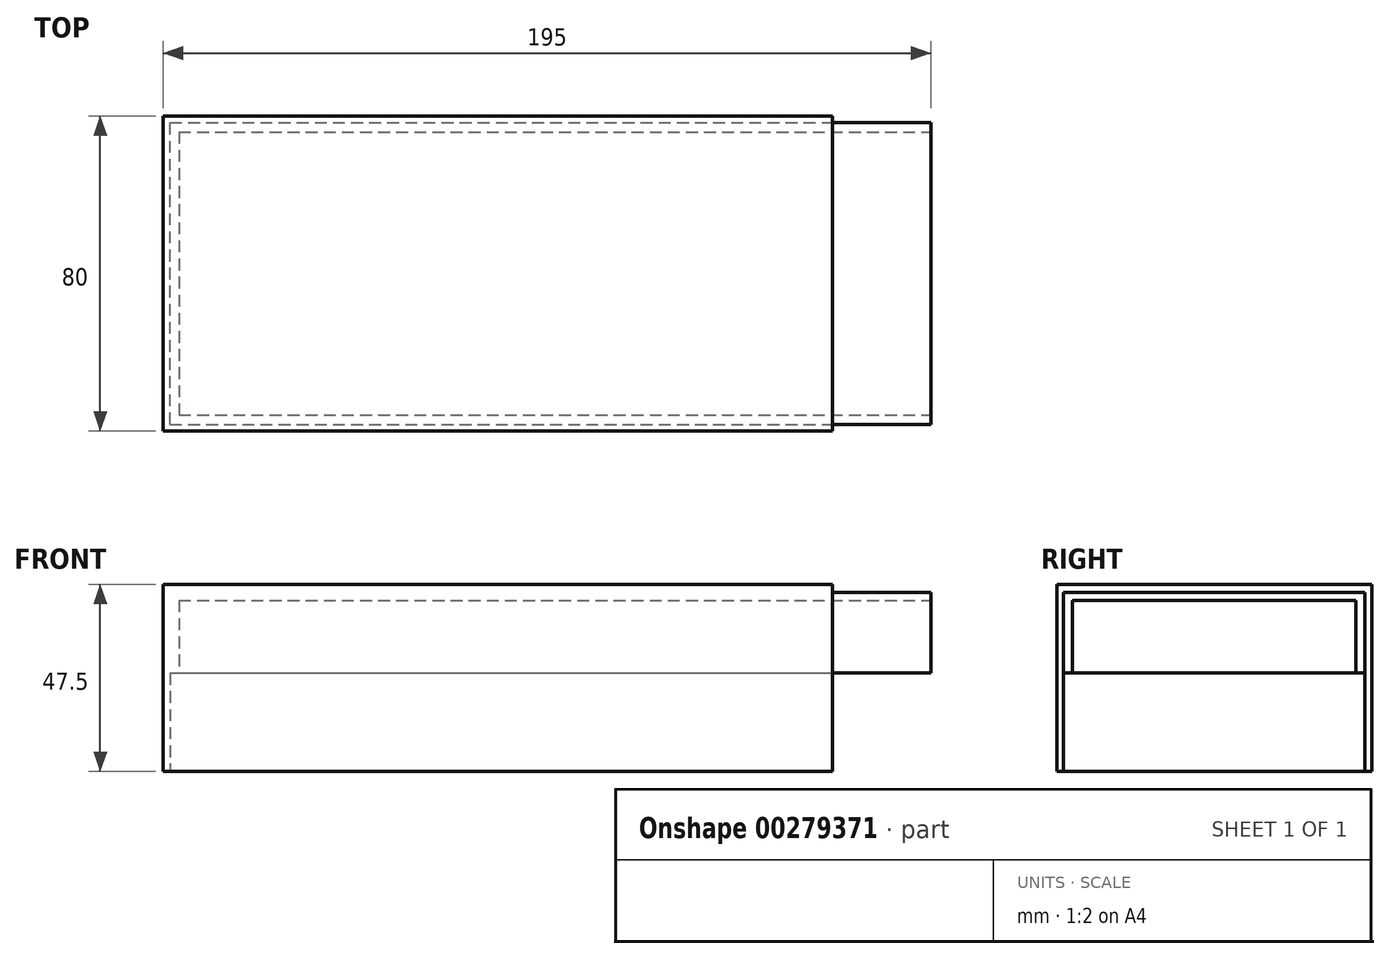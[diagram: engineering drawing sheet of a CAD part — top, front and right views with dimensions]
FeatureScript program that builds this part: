
annotation { "Feature Type Name" : "Feature", "Feature Type Description" : "" }
export const myFeature = defineFeature(function(context is Context, id is Id, definition is map)
    precondition{}
    {
        {
            var Q0;
            Q0=qCreatedBy(makeId("Top.planeOp"),FACE);
            var sketch = newSketch(context, id + "F0", { "sketchPlane" : qUnion([Q0])});
            skLineSegment(sketch, "E0", {"start": v(-189.63, 0) * mm, "end": v(207.94, 0) * mm, "construction": true});
            skLineSegment(sketch, "E1", {"start": v(0, 67.33) * mm, "end": v(0, -76.99) * mm, "construction": true});
            skLineSegment(sketch, "E2.0", {"start": v(-166, 36) * mm, "end": v(0, 36) * mm});
            skLineSegment(sketch, "E3.0", {"start": v(-166, 36) * mm, "end": v(-166, 0) * mm});
            skLineSegment(sketch, "E4.MirrorCS", {"start": v(-166, -36) * mm, "end": v(-166, 0) * mm});
            skLineSegment(sketch, "E5.MirrorCS", {"start": v(-166, -36) * mm, "end": v(0, -36) * mm});
            skLineSegment(sketch, "E6.0", {"start": v(-170, 40) * mm, "end": v(0, 40) * mm});
            skLineSegment(sketch, "E7.0", {"start": v(-170, 40) * mm, "end": v(-170, -40) * mm});
            skLineSegment(sketch, "E8.0", {"start": v(-170, -40) * mm, "end": v(0, -40) * mm});
            skLineSegment(sketch, "E9", {"start": v(0, 40) * mm, "end": v(0, 36) * mm});
            skLineSegment(sketch, "E10", {"start": v(0, -36) * mm, "end": v(0, -40) * mm});
            skLineSegment(sketch, "E11", {"start": v(0, 36) * mm, "end": v(0, -36) * mm});
            skSolve(sketch);
        }
        {
            var Q0;
            Q0=makeQuery(id+"F0.imprint","IMPRINT",FACE,{"disambiguationData":[TD([[makeQuery(id+"F0.imprint","IMPRINT",EDGE,{"derivedFrom":sQuery(id+"F0.wireOp",EDGE,"E2.0")}),1.0]])]});
            extrude(context, id + "F1", {"entities" : qUnion([Q0]), "depth" : 43.5 * mm, "offsetDistance" : 25 * mm});
        }
        {
            var Q0;
            Q0=makeQuery(id+"F1.opExtrude","CAP_FACE",FACE,{"disambiguationData":[OSD([sQuery(id+"F0.wireOp",EDGE,"E2.0"),sQuery(id+"F0.wireOp",EDGE,"E3.0"),sQuery(id+"F0.wireOp",EDGE,"E4.MirrorCS"),sQuery(id+"F0.wireOp",EDGE,"E5.MirrorCS"),sQuery(id+"F0.wireOp",EDGE,"E6.0"),sQuery(id+"F0.wireOp",EDGE,"E7.0"),sQuery(id+"F0.wireOp",EDGE,"E8.0"),sQuery(id+"F0.wireOp",EDGE,"E9"),sQuery(id+"F0.wireOp",EDGE,"E10")])],"isStart":false});
            var sketch = newSketch(context, id + "F2", { "sketchPlane" : qUnion([Q0])});
            skLineSegment(sketch, "E12.0", {"start": v(-170, 40) * mm, "end": v(0, 40) * mm});
            skLineSegment(sketch, "E13.0", {"start": v(-170, 40) * mm, "end": v(-170, -40) * mm});
            skLineSegment(sketch, "E14.0", {"start": v(-170, -40) * mm, "end": v(0, -40) * mm});
            skLineSegment(sketch, "E15", {"start": v(0, 40) * mm, "end": v(0, -40) * mm});
            skSolve(sketch);
        }
        {
            var Q0;
            Q0=qSketchRegion(id+"F2",true);
            extrude(context, id + "F3", {"entities" : qUnion([Q0]), "operationType" : NewBodyOperationType.ADD, "depth" : 4 * mm, "offsetDistance" : 25 * mm});
        }
        {
            var Q0;
            Q0=makeQuery(id+"F0.imprint","IMPRINT",FACE,{"disambiguationData":[TD([[makeQuery(id+"F0.imprint","IMPRINT",EDGE,{"derivedFrom":sQuery(id+"F0.wireOp",EDGE,"E2.0")}),1.0]])]});
            var sketch = newSketch(context, id + "F4", { "sketchPlane" : qUnion([Q0])});
            skLineSegment(sketch, "E16.0", {"start": v(-166, -36) * mm, "end": v(0, -36) * mm});
            skLineSegment(sketch, "E17.0", {"start": v(-166, -36) * mm, "end": v(-166, 36) * mm});
            skLineSegment(sketch, "E18.0", {"start": v(-166, 36) * mm, "end": v(0, 36) * mm});
            skLineSegment(sketch, "E19.0", {"start": v(-168, -38) * mm, "end": v(0, -38) * mm});
            skLineSegment(sketch, "E20.0", {"start": v(-168, 38) * mm, "end": v(0, 38) * mm});
            skLineSegment(sketch, "E21.0", {"start": v(-168, -38) * mm, "end": v(-168, 38) * mm});
            skPoint(sketch, "E22.orphan", {"position": v(-166, 0) * mm});
            skLineSegment(sketch, "E23.0", {"start": v(0, -36) * mm, "end": v(0, -38) * mm});
            skLineSegment(sketch, "E24.0", {"start": v(0, 38) * mm, "end": v(0, 36) * mm});
            skPoint(sketch, "E25.orphan", {"position": v(0, 36) * mm});
            skPoint(sketch, "E26.orphan", {"position": v(0, 40) * mm});
            skPoint(sketch, "E27.orphan", {"position": v(0, -40) * mm});
            skSolve(sketch);
        }
        {
            var Q0;
            {var subQ3=sQuery(id+"F4.wireOp",EDGE,"E16.0");Q0=makeQuery(id+"F4.imprint","IMPRINT",FACE,{"disambiguationData":[TD([[makeQuery(id+"F4.imprint","IMPRINT",EDGE,{"derivedFrom":subQ3}),-1.0]])]});}
            extrude(context, id + "F5", {"entities" : qUnion([Q0]), "operationType" : NewBodyOperationType.REMOVE, "depth" : 25 * mm, "offsetDistance" : 25 * mm});
        }
        {
            var Q0;
            Q0=makeQuery(id+"F0.imprint","IMPRINT",FACE,{"disambiguationData":[TD([[makeQuery(id+"F0.imprint","IMPRINT",EDGE,{"derivedFrom":sQuery(id+"F0.wireOp",EDGE,"E2.0")}),1.0]])]});
            var sketch = newSketch(context, id + "F6", { "sketchPlane" : qUnion([Q0])});
            skLineSegment(sketch, "E28.0", {"start": v(0, 38) * mm, "end": v(0, -38) * mm});
            skLineSegment(sketch, "E29.0", {"start": v(-25, -38) * mm, "end": v(0, -38) * mm});
            skLineSegment(sketch, "E30.0", {"start": v(-25, 38) * mm, "end": v(-25, -38) * mm});
            skPoint(sketch, "E31.orphan", {"position": v(0, -76.99) * mm});
            skPoint(sketch, "E32.orphan", {"position": v(-168, -38) * mm});
            skLineSegment(sketch, "E33.0", {"start": v(-25, 38) * mm, "end": v(0, 38) * mm});
            skPoint(sketch, "E34.orphan", {"position": v(-168, 38) * mm});
            skPoint(sketch, "E35.orphan", {"position": v(0, 67.33) * mm});
            skSolve(sketch);
        }
        {
            var Q0;
            {var subQ3=sQuery(id+"F6.wireOp",EDGE,"E29.0");Q0=makeQuery(id+"F6.imprint","IMPRINT",FACE,{"disambiguationData":[TD([[makeQuery(id+"F6.imprint","IMPRINT",EDGE,{"derivedFrom":subQ3}),1.0]])]});}
            var Q1;
            {var subQ0=sQuery(id+"F6.wireOp",EDGE,"E28.0");var subQ1=makeQuery(id+"F0.imprint","IMPRINT",EDGE,{"derivedFrom":sQuery(id+"F0.wireOp",EDGE,"E2.0")});var subQ2=makeQuery(id+"F6.imprint","INTERSECT",VERTEX,{"derivedFrom":[subQ1,subQ0]});Q1=makeQuery(id+"F6.imprint","IMPRINT",FACE,{"disambiguationData":[TD([[makeQuery(id+"F6.imprint","IMPRINT",EDGE,{"disambiguationData":[TD([[subQ2,-1.0]])],"derivedFrom":subQ0}),-1.0]])]});}
            var Q2;
            {var subQ3=sQuery(id+"F6.wireOp",EDGE,"E33.0");Q2=makeQuery(id+"F6.imprint","IMPRINT",FACE,{"disambiguationData":[TD([[makeQuery(id+"F6.imprint","IMPRINT",EDGE,{"derivedFrom":subQ3}),-1.0]])]});}
            extrude(context, id + "F7", {"entities" : qUnion([Q0, Q1, Q2]), "operationType" : NewBodyOperationType.REMOVE, "depth" : 43.5 * mm, "offsetDistance" : 25 * mm});
        }
        {
            var Q0;
            Q0=makeQuery(id+"F1.opExtrude","CAP_FACE",FACE,{"disambiguationData":[OSD([sQuery(id+"F0.wireOp",EDGE,"E2.0"),sQuery(id+"F0.wireOp",EDGE,"E3.0"),sQuery(id+"F0.wireOp",EDGE,"E4.MirrorCS"),sQuery(id+"F0.wireOp",EDGE,"E5.MirrorCS"),sQuery(id+"F0.wireOp",EDGE,"E6.0"),sQuery(id+"F0.wireOp",EDGE,"E7.0"),sQuery(id+"F0.wireOp",EDGE,"E8.0"),sQuery(id+"F0.wireOp",EDGE,"E9"),sQuery(id+"F0.wireOp",EDGE,"E10")])],"isStart":true});
            var sketch = newSketch(context, id + "F8", { "sketchPlane" : qUnion([Q0])});
            skLineSegment(sketch, "E36.0", {"start": v(-168, 38) * mm, "end": v(0, 38) * mm});
            skLineSegment(sketch, "E37.0", {"start": v(-168, 38) * mm, "end": v(-168, -38) * mm});
            skLineSegment(sketch, "E38.0", {"start": v(-168, -38) * mm, "end": v(0, -38) * mm});
            skLineSegment(sketch, "E39.0", {"start": v(0, 38) * mm, "end": v(0, 38.3) * mm});
            skLineSegment(sketch, "E40.0", {"start": v(0, -38.3) * mm, "end": v(0, -38) * mm});
            skLineSegment(sketch, "E41.0", {"start": v(-168.3, 38.3) * mm, "end": v(0, 38.3) * mm});
            skLineSegment(sketch, "E42.0", {"start": v(-168.3, 38.3) * mm, "end": v(-168.3, -38.3) * mm});
            skLineSegment(sketch, "E43.0", {"start": v(-168.3, -38.3) * mm, "end": v(0, -38.3) * mm});
            skPoint(sketch, "E44.orphan", {"position": v(0, -40) * mm});
            skPoint(sketch, "E45.orphan", {"position": v(0, 40) * mm});
            skSolve(sketch);
        }
        {
            var Q0;
            Q0=makeQuery(id+"F8.imprint","IMPRINT",FACE,{"disambiguationData":[TD([[makeQuery(id+"F8.imprint","IMPRINT",EDGE,{"derivedFrom":sQuery(id+"F8.wireOp",EDGE,"E36.0")}),1.0]])]});
            extrude(context, id + "F9", {"entities" : qUnion([Q0]), "operationType" : NewBodyOperationType.REMOVE, "oppositeDirection" : true, "depth" : 25 * mm, "offsetDistance" : 25 * mm});
        }
        {
            var Q0;
            Q0=makeQuery(id+"F9.boolean.opBoolean","MERGE",FACE,{"derivedFrom":[makeQuery(id+"F5.boolean.opBoolean","COPY",FACE,{"derivedFrom":makeQuery(id+"F5.opExtrude","CAP_FACE",FACE,{"disambiguationData":[OSD([sQuery(id+"F4.wireOp",EDGE,"E16.0"),sQuery(id+"F4.wireOp",EDGE,"E17.0"),sQuery(id+"F4.wireOp",EDGE,"E18.0"),sQuery(id+"F4.wireOp",EDGE,"E19.0"),sQuery(id+"F4.wireOp",EDGE,"E20.0"),sQuery(id+"F4.wireOp",EDGE,"E21.0"),sQuery(id+"F4.wireOp",EDGE,"E23.0"),sQuery(id+"F4.wireOp",EDGE,"E24.0")])],"isStart":false})}),makeQuery(id+"F9.opExtrude","CAP_FACE",FACE,{"disambiguationData":[OSD([sQuery(id+"F8.wireOp",EDGE,"E36.0"),sQuery(id+"F8.wireOp",EDGE,"E37.0"),sQuery(id+"F8.wireOp",EDGE,"E38.0"),sQuery(id+"F8.wireOp",EDGE,"E39.0"),sQuery(id+"F8.wireOp",EDGE,"E40.0"),sQuery(id+"F8.wireOp",EDGE,"E41.0"),sQuery(id+"F8.wireOp",EDGE,"E42.0"),sQuery(id+"F8.wireOp",EDGE,"E43.0")])],"isStart":false})]});
            var sketch = newSketch(context, id + "F10", { "sketchPlane" : qUnion([Q0])});
            skLineSegment(sketch, "E46.0", {"start": v(-25, 38) * mm, "end": v(0, 38) * mm});
            skLineSegment(sketch, "E47.0", {"start": v(-168.3, 38.3) * mm, "end": v(0, 38.3) * mm});
            skLineSegment(sketch, "E48.0", {"start": v(-25, 38.3) * mm, "end": v(-25, 38) * mm});
            skPoint(sketch, "E49.orphan", {"position": v(-25, 36) * mm});
            skLineSegment(sketch, "E50", {"start": v(0, 38.3) * mm, "end": v(0, 38) * mm});
            skSolve(sketch);
        }
        {
            var Q0;
            Q0=qSketchRegion(id+"F10",true);
            extrude(context, id + "F11", {"entities" : qUnion([Q0]), "operationType" : NewBodyOperationType.REMOVE, "oppositeDirection" : true, "depth" : (43.5 - 25) * mm, "offsetDistance" : 25 * mm});
        }
        {
            var Q0;
            Q0=makeQuery(id+"F9.boolean.opBoolean","MERGE",FACE,{"derivedFrom":[makeQuery(id+"F5.boolean.opBoolean","COPY",FACE,{"derivedFrom":makeQuery(id+"F5.opExtrude","CAP_FACE",FACE,{"disambiguationData":[OSD([sQuery(id+"F4.wireOp",EDGE,"E16.0"),sQuery(id+"F4.wireOp",EDGE,"E17.0"),sQuery(id+"F4.wireOp",EDGE,"E18.0"),sQuery(id+"F4.wireOp",EDGE,"E19.0"),sQuery(id+"F4.wireOp",EDGE,"E20.0"),sQuery(id+"F4.wireOp",EDGE,"E21.0"),sQuery(id+"F4.wireOp",EDGE,"E23.0"),sQuery(id+"F4.wireOp",EDGE,"E24.0")])],"isStart":false})}),makeQuery(id+"F9.opExtrude","CAP_FACE",FACE,{"disambiguationData":[OSD([sQuery(id+"F8.wireOp",EDGE,"E36.0"),sQuery(id+"F8.wireOp",EDGE,"E37.0"),sQuery(id+"F8.wireOp",EDGE,"E38.0"),sQuery(id+"F8.wireOp",EDGE,"E39.0"),sQuery(id+"F8.wireOp",EDGE,"E40.0"),sQuery(id+"F8.wireOp",EDGE,"E41.0"),sQuery(id+"F8.wireOp",EDGE,"E42.0"),sQuery(id+"F8.wireOp",EDGE,"E43.0")])],"isStart":false})]});
            var sketch = newSketch(context, id + "F12", { "sketchPlane" : qUnion([Q0])});
            skLineSegment(sketch, "E51.0", {"start": v(-25, 38.3) * mm, "end": v(0, 38.3) * mm});
            skPoint(sketch, "E52.orphan", {"position": v(-168.3, 38.3) * mm});
            skPoint(sketch, "E53.orphan", {"position": v(0, -38) * mm});
            skLineSegment(sketch, "E54.1", {"start": v(-25, -38) * mm, "end": v(0, -38) * mm});
            skLineSegment(sketch, "E55.0", {"start": v(0, -38) * mm, "end": v(0, -36) * mm});
            skLineSegment(sketch, "E56.0", {"start": v(-25, -36) * mm, "end": v(-25, -38) * mm});
            skLineSegment(sketch, "E57", {"start": v(-25, -36) * mm, "end": v(0, -36) * mm});
            skLineSegment(sketch, "E58.0", {"start": v(-25, 38.3) * mm, "end": v(-25, 36) * mm});
            skLineSegment(sketch, "E59", {"start": v(-25, 36) * mm, "end": v(0, 36) * mm});
            skLineSegment(sketch, "E60", {"start": v(0, 36) * mm, "end": v(0, 38.3) * mm});
            skSolve(sketch);
        }
        {
            var Q0;
            Q0 = qSketchRegion(id + "F12", true);
            extrude(context, id + "F13", {"entities" : qUnion([Q0]), "operationType" : NewBodyOperationType.ADD, "oppositeDirection" : true, "depth" : (43.5 - 25) * mm, "offsetDistance" : 25 * mm});
        }
        {
            var Q0;
            Q0=makeQuery(id+"F13.boolean.opBoolean","MERGE",FACE,{"derivedFrom":[makeQuery(id+"F3.boolean.opBoolean","MERGE",FACE,{"derivedFrom":[makeQuery(id+"F1.opExtrude","SWEPT_FACE",FACE,{"disambiguationData":[OSD([sQuery(id+"F0.wireOp",EDGE,"E9")])]}),makeQuery(id+"F1.opExtrude","SWEPT_FACE",FACE,{"disambiguationData":[OSD([sQuery(id+"F0.wireOp",EDGE,"E10")])]}),makeQuery(id+"F3.opExtrude","SWEPT_FACE",FACE,{"disambiguationData":[OSD([sQuery(id+"F2.wireOp",EDGE,"E15")])]})]}),makeQuery(id+"F13.opExtrude","SWEPT_FACE",FACE,{"disambiguationData":[OSD([sQuery(id+"F12.wireOp",EDGE,"E55.0")])]}),makeQuery(id+"F13.opExtrude","SWEPT_FACE",FACE,{"disambiguationData":[OSD([sQuery(id+"F12.wireOp",EDGE,"7b1d7395-10de-43ad-be49-9ea8bce619b3.trimOffspring")])]})]});
            var sketch = newSketch(context, id + "F14", { "sketchPlane" : qUnion([Q0])});
            skLineSegment(sketch, "E61.0", {"start": v(36, 43.5) * mm, "end": v(-36, 43.5) * mm});
            skLineSegment(sketch, "E62.0", {"start": v(36, 43.5) * mm, "end": v(36, 25) * mm});
            skLineSegment(sketch, "E63.0", {"start": v(-38.3, 45.5) * mm, "end": v(-38.3, 25) * mm});
            skLineSegment(sketch, "E64.0", {"start": v(-38.3, 0) * mm, "end": v(-40, 0) * mm});
            skLineSegment(sketch, "E65.0", {"start": v(40, 0) * mm, "end": v(38.3, 0) * mm});
            skLineSegment(sketch, "E66.0", {"start": v(38.3, 25) * mm, "end": v(36, 25) * mm});
            skPoint(sketch, "E67.0.start.orphan", {"position": v(-40, 47.5) * mm});
            skPoint(sketch, "E68.orphan", {"position": v(40, 47.5) * mm});
            skLineSegment(sketch, "E69.0", {"start": v(-36, 25) * mm, "end": v(-38.3, 25) * mm});
            skLineSegment(sketch, "E70.0", {"start": v(-36, 43.5) * mm, "end": v(-36, 25) * mm});
            skLineSegment(sketch, "E71", {"start": v(38.3, 25) * mm, "end": v(38.3, 45.5) * mm});
            skLineSegment(sketch, "E72.0", {"start": v(38.3, 45.5) * mm, "end": v(-38.3, 45.5) * mm});
            skSolve(sketch);
        }
        {
            var Q0;
            Q0 = qSketchRegion(id + "F14", true);
            extrude(context, id + "F15", {"entities" : qUnion([Q0]), "operationType" : NewBodyOperationType.ADD, "depth" : 25 * mm, "offsetDistance" : 25 * mm});
        }
    });
